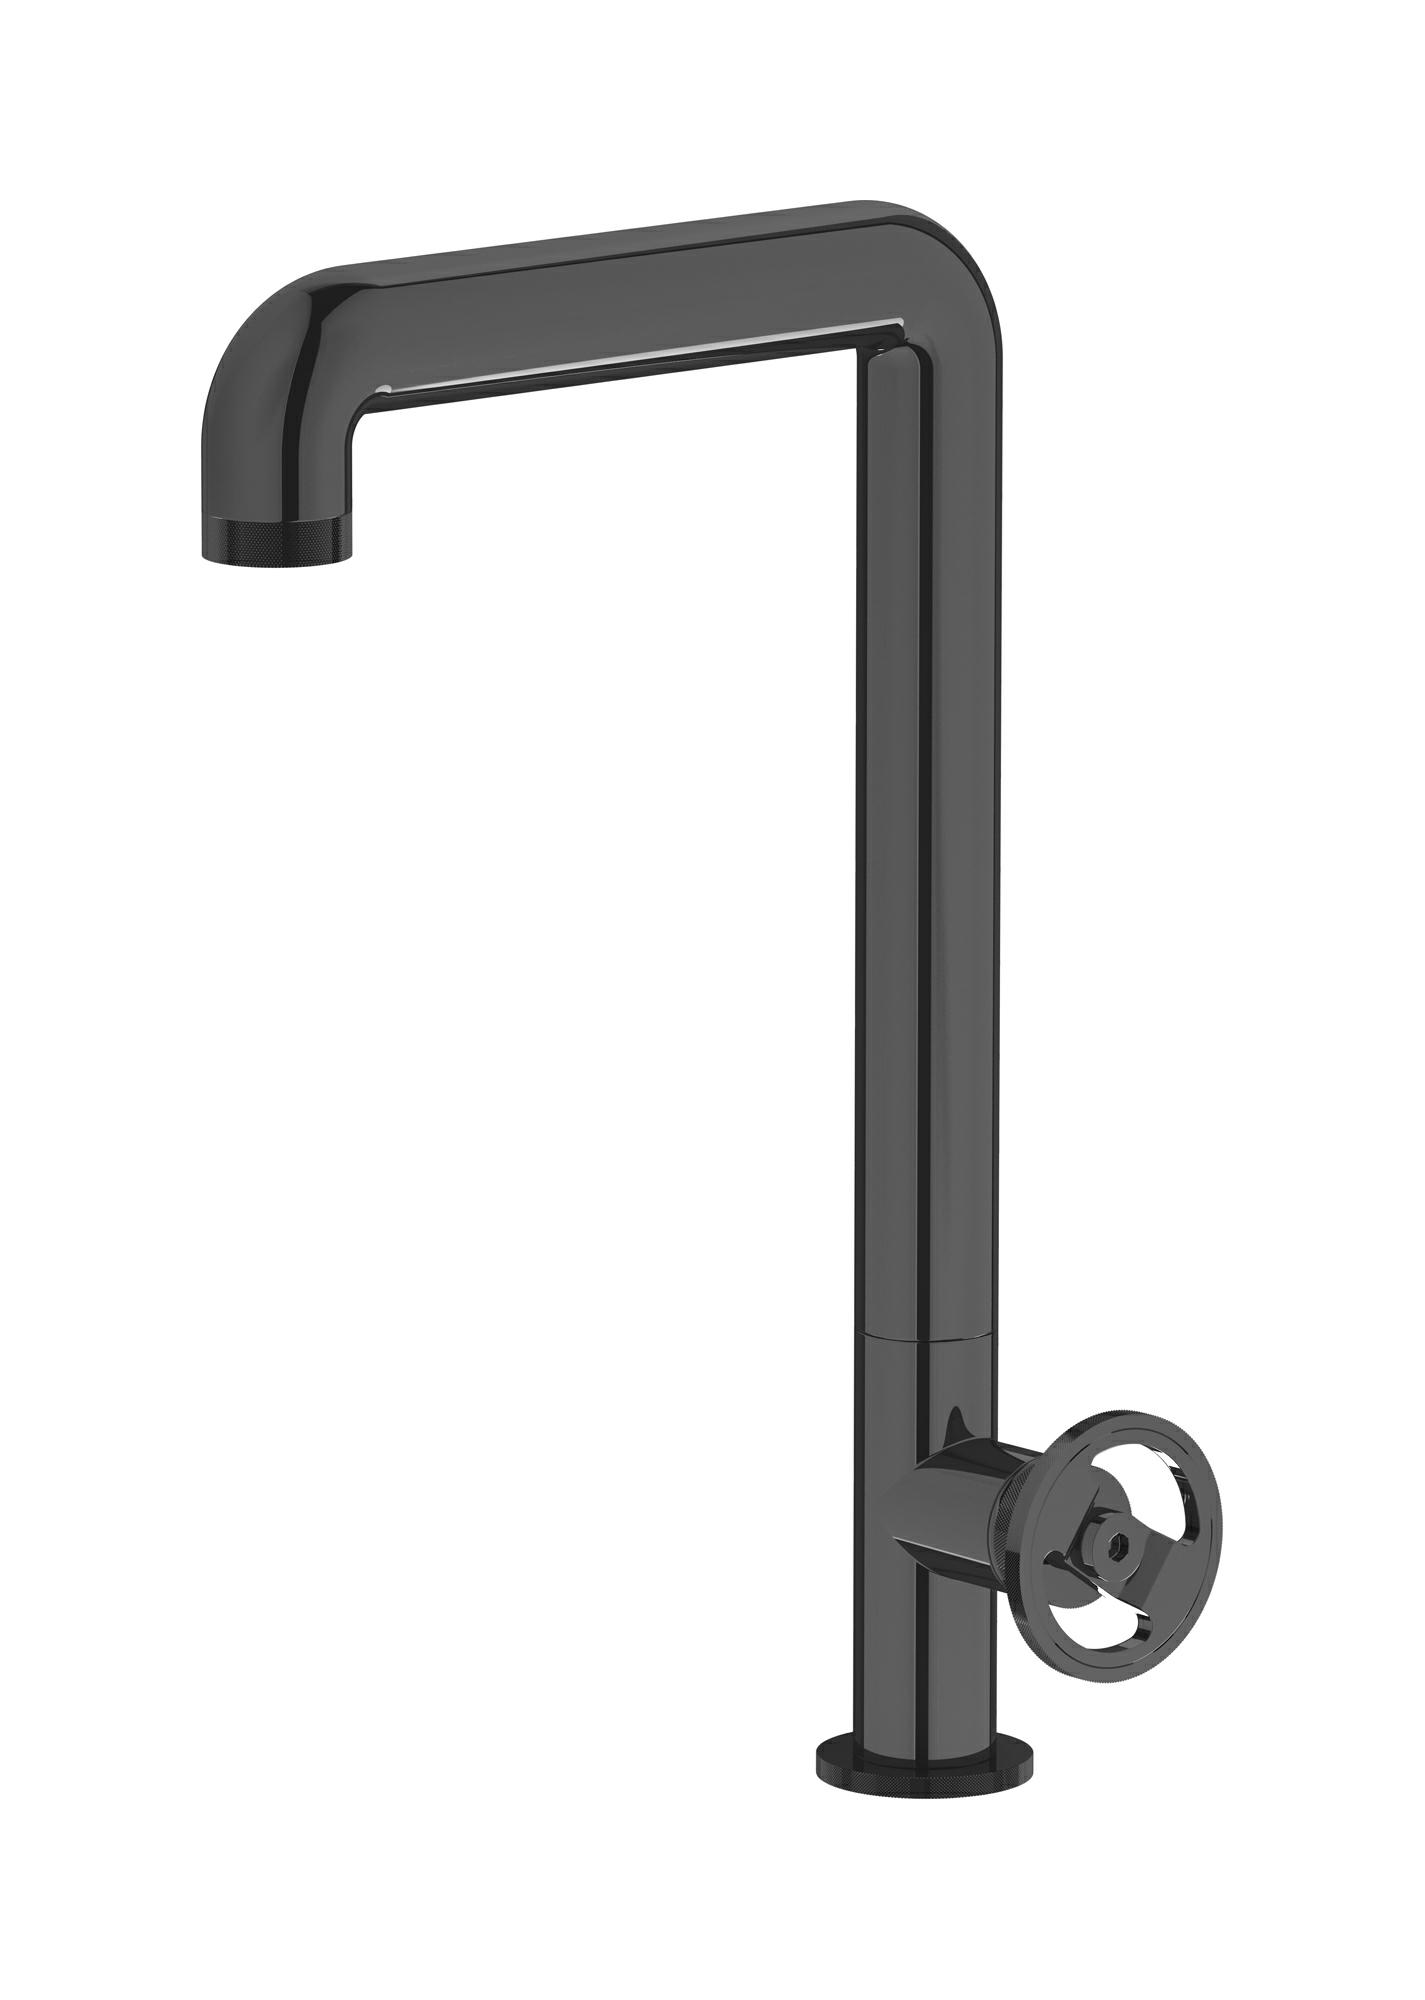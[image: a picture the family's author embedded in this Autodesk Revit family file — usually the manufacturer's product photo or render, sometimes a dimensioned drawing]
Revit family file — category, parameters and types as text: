
# Revit family: B1370
name_source: partatom
category: Apparecchi idraulici
units: mm (PartAtom-declared; Revit-internal decimal feet)

## family parameters
Basato su piano di lavoro = No
Condiviso = No
Mantieni orientamento annotazione = No
Numero OmniClass = 23.45.55.17
Punto di calcolo locali = No
Quota connettore circolare = Usa diametro
Sempre verticale = Sì
Taglio con vuoti quando caricato = No
Tipo di parte = Normale
Titolo OmniClass = Mixing Faucets

## types (13) — shared parameters
Cold water inlet = 10 mm  [stored 0.0328084 ft]
Commenti sul tipo = Single lever kitchen mixer
Connessione CW = No
Connessione HW = No
Connessione di scarico = No
Connessione di ventilazione = No
Descrizione = Single lever kitchen mixer
Hot water inlet = 10 mm  [stored 0.0328084 ft]
Produttore = IB Rubinetterie S.p.A.
URL = https://www.weareib.it
zero-valued in all types: Prospetto di default

## per-type parameters (varying)
| type | Finishes surface | Immagine tipo | Modello |
| Chrome | IB_Chrome | B1370CC.jpg | B1370CC |
| Black Chrome | IB_Black chrome | B1370CF.jpg | B1370CF |
| Brushed Black Chrome | IB_Brushed black chrome | B1370CS.jpg | B1370CS |
| Pale Gold | IB_Pale gold | B1370II.jpg | B1370II |
| Brushed Pale Gold | IB_brushed pale gold | B1370IS.jpg | B1370IS |
| Matt Black | IB_matt black | B1370NP.jpg | B1370NP |
| Natural Brass | IB_Brass | B1370ON.jpg | B1370ON |
| Gold | IB_gold | B1370OO.jpg | B1370OO |
| Brushed Gold | IB_brushed gold | B1370OS.jpg | B1370OS |
| Rose Gold | IB_Rose gold | B1370RS.jpg | B1370RS |
| Brushed Rose Gold | IB_Brushed rose gold | B1370SR.jpg | B1370SR |
| Brushed Nickel | IB_Brushed nickel | B1370SS.jpg | B1370SS |
| Modern Bronze | IB_Modern bronze | B1370CC.jpg | B1370MB |

note: [stored X ft] marks values corroborated as IEEE doubles in the binary element streams (Revit-internal decimal feet)
